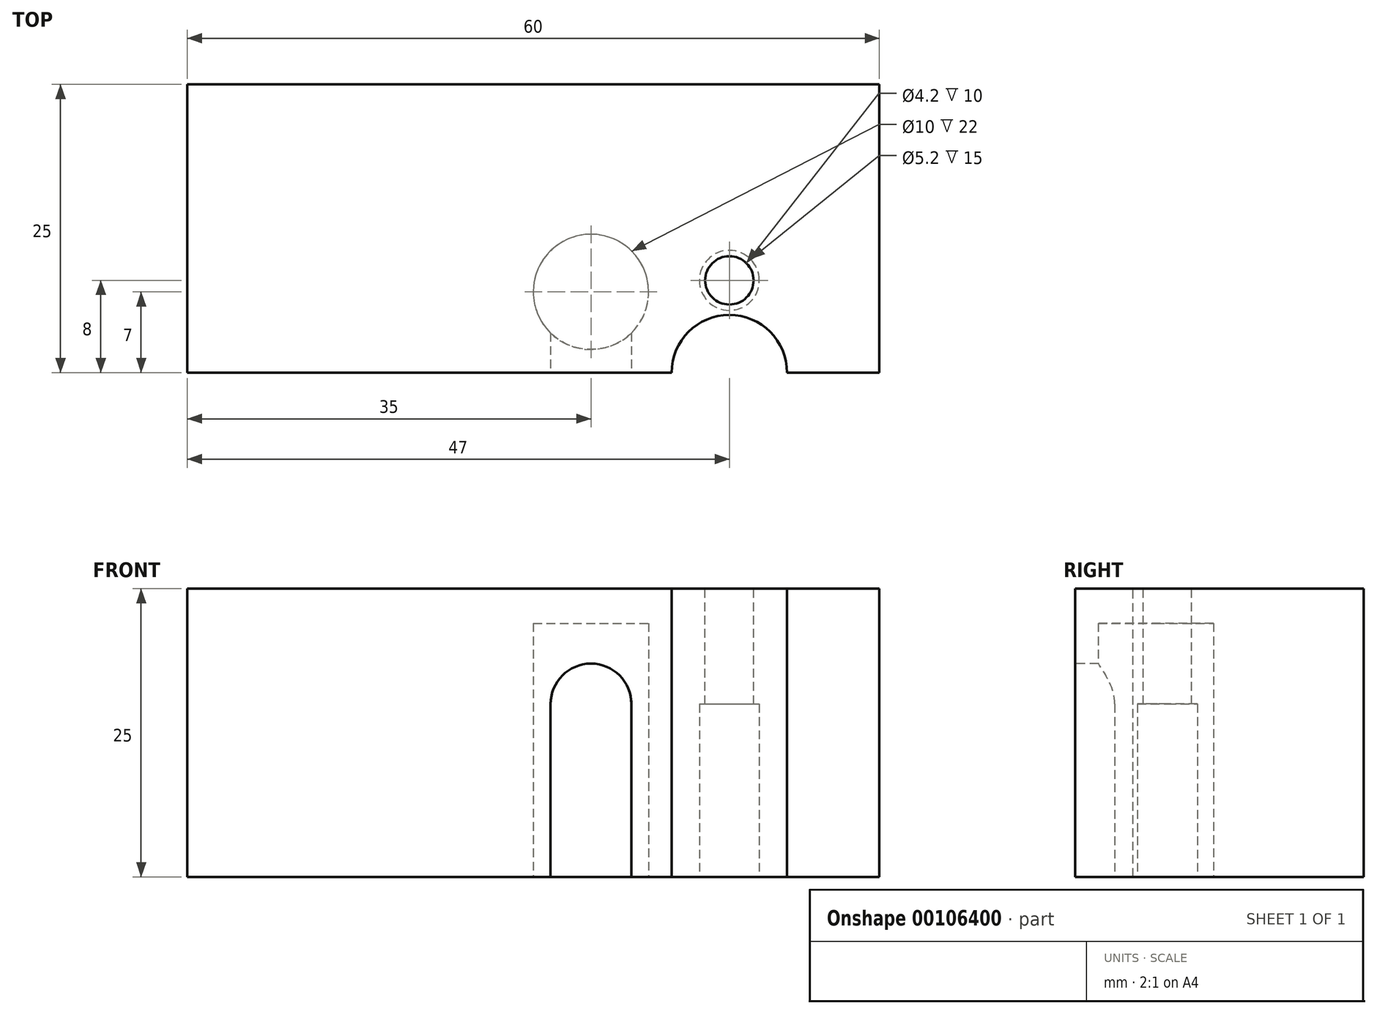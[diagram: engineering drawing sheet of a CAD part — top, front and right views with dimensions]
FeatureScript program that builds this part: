
annotation { "Feature Type Name" : "Feature", "Feature Type Description" : "" }
export const myFeature = defineFeature(function(context is Context, id is Id, definition is map)
    precondition{}
    {
        {
            var Q0;
            Q0=qCreatedBy(makeId("Right.planeOp"),FACE);
            var sketch = newSketch(context, id + "F0", { "sketchPlane" : qUnion([Q0])});
            skLineSegment(sketch, "E0.bottom", {"start": v(12.5, -12.5) * mm, "end": v(-12.5, -12.5) * mm});
            skLineSegment(sketch, "E0.top", {"start": v(12.5, 12.5) * mm, "end": v(-12.5, 12.5) * mm});
            skLineSegment(sketch, "E0.left", {"start": v(12.5, -12.5) * mm, "end": v(12.5, 12.5) * mm});
            skLineSegment(sketch, "E0.right", {"start": v(-12.5, -12.5) * mm, "end": v(-12.5, 12.5) * mm});
            skPoint(sketch, "E0.middle", {"position": v(0, 0) * mm});
            skSolve(sketch);
        }
        {
            var Q0;
            Q0=makeQuery(id+"F0.imprint","IMPRINT",FACE,{"disambiguationData":[TD([[makeQuery(id+"F0.imprint","IMPRINT",EDGE,{"derivedFrom":sQuery(id+"F0.wireOp",EDGE,"E0.bottom")}),-1.0]])]});
            extrude(context, id + "F1", {"entities" : qUnion([Q0]), "depth" : 60 * mm, "symmetric" : true});
        }
        {
            var Q0;
            Q0=makeQuery(id+"F1.opExtrude","SWEPT_FACE",FACE,{"disambiguationData":[OSD([sQuery(id+"F0.wireOp",EDGE,"E0.top")])]});
            var sketch = newSketch(context, id + "F2", { "sketchPlane" : qUnion([Q0])});
            skArc(sketch, "E1", {"start": v(22, -12.5) * mm, "mid": v(17, -7.5) * mm, "end": v(12, -12.5) * mm});
            skLineSegment(sketch, "E2", {"start": v(12, -12.5) * mm, "end": v(22, -12.5) * mm});
            skSolve(sketch);
        }
        {
            var Q0;
            Q0=makeQuery(id+"F2.imprint","IMPRINT",FACE,{"disambiguationData":[TD([[makeQuery(id+"F2.imprint","IMPRINT",EDGE,{"derivedFrom":sQuery(id+"F2.wireOp",EDGE,"E1")}),1.0]])]});
            extrude(context, id + "F3", {"entities" : qUnion([Q0]), "operationType" : NewBodyOperationType.REMOVE, "endBound" : BoundingType.THROUGH_ALL, "oppositeDirection" : true, "depth" : 25 * mm});
        }
        {
            var Q0;
            Q0=makeQuery(id+"F1.opExtrude","SWEPT_FACE",FACE,{"disambiguationData":[OSD([sQuery(id+"F0.wireOp",EDGE,"E0.top")])]});
            var sketch = newSketch(context, id + "F4", { "sketchPlane" : qUnion([Q0])});
            skCircle(sketch, "E3", {"center": v(17, -4.5) * mm, "radius": 2.1 * mm});
            skPoint(sketch, "E4", {"position": v(17, -7.5) * mm});
            skSolve(sketch);
        }
        {
            var Q0;
            Q0=makeQuery(id+"F4.imprint","IMPRINT",FACE,{"disambiguationData":[TD([[makeQuery(id+"F4.imprint","IMPRINT",EDGE,{"derivedFrom":sQuery(id+"F4.wireOp",EDGE,"E3")}),1.0]])]});
            extrude(context, id + "F5", {"entities" : qUnion([Q0]), "operationType" : NewBodyOperationType.REMOVE, "endBound" : BoundingType.THROUGH_ALL, "oppositeDirection" : true, "depth" : 25 * mm});
        }
        {
            var Q0;
            Q0=makeQuery(id+"F1.opExtrude","SWEPT_FACE",FACE,{"disambiguationData":[OSD([sQuery(id+"F0.wireOp",EDGE,"E0.bottom")])]});
            var sketch = newSketch(context, id + "F6", { "sketchPlane" : qUnion([Q0])});
            skCircle(sketch, "E5", {"center": v(5, 5.5) * mm, "radius": 5 * mm});
            skLineSegment(sketch, "E6", {"start": v(17, 12.5) * mm, "end": v(17, 0) * mm, "construction": true});
            skPoint(sketch, "E6.endSnap0", {"position": v(17, 7.5) * mm});
            skSolve(sketch);
        }
        {
            var Q0;
            Q0=makeQuery(id+"F6.imprint","IMPRINT",FACE,{"disambiguationData":[TD([[makeQuery(id+"F6.imprint","IMPRINT",EDGE,{"derivedFrom":sQuery(id+"F6.wireOp",EDGE,"E5")}),1.0]])]});
            extrude(context, id + "F7", {"entities" : qUnion([Q0]), "operationType" : NewBodyOperationType.REMOVE, "oppositeDirection" : true, "depth" : 22 * mm});
        }
        {
            var Q0;
            {var subQ0=sQuery(id+"F0.wireOp",EDGE,"E0.bottom");var subQ1=sQuery(id+"F0.wireOp",EDGE,"E0.right");var subQ2=sQuery(id+"F0.wireOp",EDGE,"E0.top");Q0=makeQuery(id+"F3.boolean.opBoolean","SPLIT",FACE,{"disambiguationData":[TD([makeQuery(id+"F1.opExtrude","CAP_FACE",FACE,{"disambiguationData":[OSD([subQ0,subQ2,sQuery(id+"F0.wireOp",EDGE,"E0.left"),subQ1])],"isStart":true})])],"derivedFrom":makeQuery(id+"F1.opExtrude","SWEPT_FACE",FACE,{"disambiguationData":[OSD([subQ1])]})});}
            var sketch = newSketch(context, id + "F8", { "sketchPlane" : qUnion([Q0])});
            skLineSegment(sketch, "E7", {"start": v(8.5, -12.5) * mm, "end": v(8.5, 2.5) * mm});
            skArc(sketch, "E8", {"start": v(8.5, 2.5) * mm, "mid": v(5, 6) * mm, "end": v(1.5, 2.5) * mm});
            skLineSegment(sketch, "E9", {"start": v(1.5, 2.5) * mm, "end": v(1.5, -12.5) * mm});
            skLineSegment(sketch, "E10", {"start": v(1.5, -12.5) * mm, "end": v(8.5, -12.5) * mm});
            skSolve(sketch);
        }
        {
            var Q0;
            Q0=makeQuery(id+"F8.imprint","IMPRINT",FACE,{"disambiguationData":[TD([[makeQuery(id+"F8.imprint","IMPRINT",EDGE,{"derivedFrom":sQuery(id+"F8.wireOp",EDGE,"E7")}),1.0]])]});
            extrude(context, id + "F9", {"entities" : qUnion([Q0]), "operationType" : NewBodyOperationType.REMOVE, "oppositeDirection" : true, "depth" : 7 * mm});
        }
        {
            var Q0;
            Q0=makeQuery(id+"F1.opExtrude","SWEPT_FACE",FACE,{"disambiguationData":[OSD([sQuery(id+"F0.wireOp",EDGE,"E0.bottom")])]});
            var sketch = newSketch(context, id + "F10", { "sketchPlane" : qUnion([Q0])});
            skCircle(sketch, "E11", {"center": v(17, 4.5) * mm, "radius": 2.6 * mm});
            skSolve(sketch);
        }
        {
            var Q0;
            Q0=qSketchRegion(id+"F10",true);
            extrude(context, id + "F11", {"entities" : qUnion([Q0]), "operationType" : NewBodyOperationType.REMOVE, "oppositeDirection" : true, "depth" : 15 * mm});
        }
        {
            var Q0;
            Q0=makeQuery(id+"F1.opExtrude","SWEPT_BODY",BODY,{"disambiguationData":[OSD([sQuery(id+"F0.wireOp",EDGE,"E0.bottom"),sQuery(id+"F0.wireOp",EDGE,"E0.top"),sQuery(id+"F0.wireOp",EDGE,"E0.left"),sQuery(id+"F0.wireOp",EDGE,"E0.right")])]});
            transform(context, id + "F12", {"entities" : qUnion([Q0]), "transformType" : TransformType.TRANSLATION_3D, "dx" : 0 * mm, "dy" : 0 * mm, "dz" : 0 * mm, "makeCopy" : true});
        }
        {
            var Q0;
            Q0=makeQuery(id+"F12.opPattern","COPY",BODY,{"derivedFrom":makeQuery(id+"F1.opExtrude","SWEPT_BODY",BODY,{"disambiguationData":[OSD([sQuery(id+"F0.wireOp",EDGE,"E0.bottom"),sQuery(id+"F0.wireOp",EDGE,"E0.top"),sQuery(id+"F0.wireOp",EDGE,"E0.left"),sQuery(id+"F0.wireOp",EDGE,"E0.right")])]}),"instanceName":"1"});
            deleteBodies(context, id + "F13", {"entities" : qUnion([Q0])});
        }
    });
